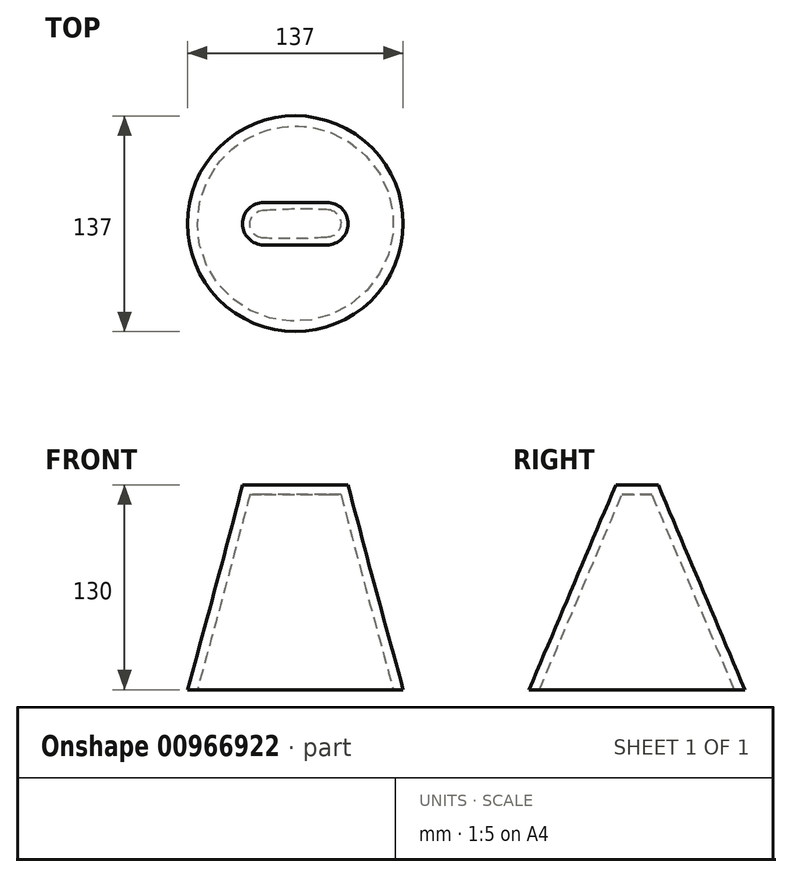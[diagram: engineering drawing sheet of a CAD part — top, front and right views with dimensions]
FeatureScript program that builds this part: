
annotation { "Feature Type Name" : "Feature", "Feature Type Description" : "" }
export const myFeature = defineFeature(function(context is Context, id is Id, definition is map)
    precondition{}
    {
        {
            var Q0;
            Q0=qCreatedBy(makeId("Top.planeOp"),FACE);
            var sketch = newSketch(context, id + "F0", { "sketchPlane" : qUnion([Q0])});
            skCircle(sketch, "E0", {"center": v(0, 0) * mm, "radius": 62.5 * mm, "construction": true});
            skCircle(sketch, "E1", {"center": v(0, 0) * mm, "radius": 65.5 * mm, "construction": true});
            skCircle(sketch, "E2", {"center": v(0, 0) * mm, "radius": 68.5 * mm});
            skSolve(sketch);
        }
        {
            var Q0;
            Q0=makeQuery(id+"F0.imprint","IMPRINT",FACE,{"disambiguationData":[TD([[makeQuery(id+"F0.imprint","IMPRINT",EDGE,{"derivedFrom":sQuery(id+"F0.wireOp",EDGE,"E2")}),1.0]])]});
            cPlane(context, id + "F1", {"entities" : qUnion([Q0]), "cplaneType" : CPlaneType.OFFSET, "offset" : 130 * mm, "width" : 150 * mm, "height" : 150 * mm});
        }
        {
            var Q0;
            Q0=qCreatedBy(id+"F1.planeOp",FACE);
            var sketch = newSketch(context, id + "F2", { "sketchPlane" : qUnion([Q0])});
            skArc(sketch, "E3", {"start": v(-20, 7.5) * mm, "mid": v(-27.5, 0) * mm, "end": v(-20, -7.5) * mm, "construction": true});
            skArc(sketch, "E4", {"start": v(20, -7.5) * mm, "mid": v(27.5, 0) * mm, "end": v(20, 7.5) * mm, "construction": true});
            skLineSegment(sketch, "E5", {"start": v(-20, 7.5) * mm, "end": v(20, 7.5) * mm, "construction": true});
            skLineSegment(sketch, "E6", {"start": v(20, -7.5) * mm, "end": v(-20, -7.5) * mm, "construction": true});
            skPoint(sketch, "E7", {"position": v(0, 7.5) * mm});
            skPoint(sketch, "E8", {"position": v(-27.5, 0) * mm});
            skPoint(sketch, "E9", {"position": v(27.5, 0) * mm});
            skArc(sketch, "E10", {"start": v(-20, 10.5) * mm, "mid": v(-30.5, 0) * mm, "end": v(-20, -10.5) * mm, "construction": true});
            skArc(sketch, "E11", {"start": v(-20, 13.5) * mm, "mid": v(-33.5, 0) * mm, "end": v(-20, -13.5) * mm});
            skArc(sketch, "E12", {"start": v(20, -10.5) * mm, "mid": v(30.5, 0) * mm, "end": v(20, 10.5) * mm, "construction": true});
            skLineSegment(sketch, "E13", {"start": v(-20, 10.5) * mm, "end": v(20, 10.5) * mm, "construction": true});
            skLineSegment(sketch, "E14", {"start": v(20, -10.5) * mm, "end": v(-20, -10.5) * mm, "construction": true});
            skLineSegment(sketch, "E15", {"start": v(-20, -13.5) * mm, "end": v(20, -13.5) * mm});
            skLineSegment(sketch, "E16", {"start": v(20, 13.5) * mm, "end": v(-20, 13.5) * mm});
            skArc(sketch, "E17.trimOffspring", {"start": v(20, -13.5) * mm, "mid": v(33.5, 0) * mm, "end": v(20, 13.5) * mm});
            skSolve(sketch);
        }
        {
            var Q0;
            Q0=makeQuery(id+"F2.imprint","IMPRINT",FACE,{"disambiguationData":[TD([[makeQuery(id+"F2.imprint","IMPRINT",EDGE,{"derivedFrom":sQuery(id+"F2.wireOp",EDGE,"E11")}),1.0]])]});
            var Q1;
            Q1=makeQuery(id+"F0.imprint","IMPRINT",FACE,{"disambiguationData":[TD([[makeQuery(id+"F0.imprint","IMPRINT",EDGE,{"derivedFrom":sQuery(id+"F0.wireOp",EDGE,"E2")}),1.0]])]});
            var Q2;
            Q2=makeQuery(id+"F2.imprint","IMPRINT",FACE,{"disambiguationData":[TD([[makeQuery(id+"F2.imprint","IMPRINT",EDGE,{"derivedFrom":sQuery(id+"F2.wireOp",EDGE,"E11")}),1.0]])]});
            var Q3;
            Q3=makeQuery(id+"F0.imprint","IMPRINT",FACE,{"disambiguationData":[TD([[makeQuery(id+"F0.imprint","IMPRINT",EDGE,{"derivedFrom":sQuery(id+"F0.wireOp",EDGE,"E2")}),1.0]])]});
            loft(context, id + "F3", {"sheetProfilesArray" : [{ "sheetProfileEntities" : qUnion([Q0]) }, { "sheetProfileEntities" : qUnion([Q1]) }], "wireProfilesArray" : [{ "wireProfileEntities" : qUnion([Q2]) }, { "wireProfileEntities" : qUnion([Q3]) }]});
        }
        {
            var Q0;
            Q0=makeQuery(id+"F3.opLoft","CAP_FACE",FACE,{"disambiguationData":[OSD([makeQuery(id+"F0.imprint","IMPRINT",FACE,{"disambiguationData":[TD([[makeQuery(id+"F0.imprint","IMPRINT",EDGE,{"derivedFrom":sQuery(id+"F0.wireOp",EDGE,"E2")}),1.0]])]})])],"isStart":true});
            shell(context, id + "F4", {"entities" : qUnion([Q0]), "thickness" : 6 * mm});
        }
    });
